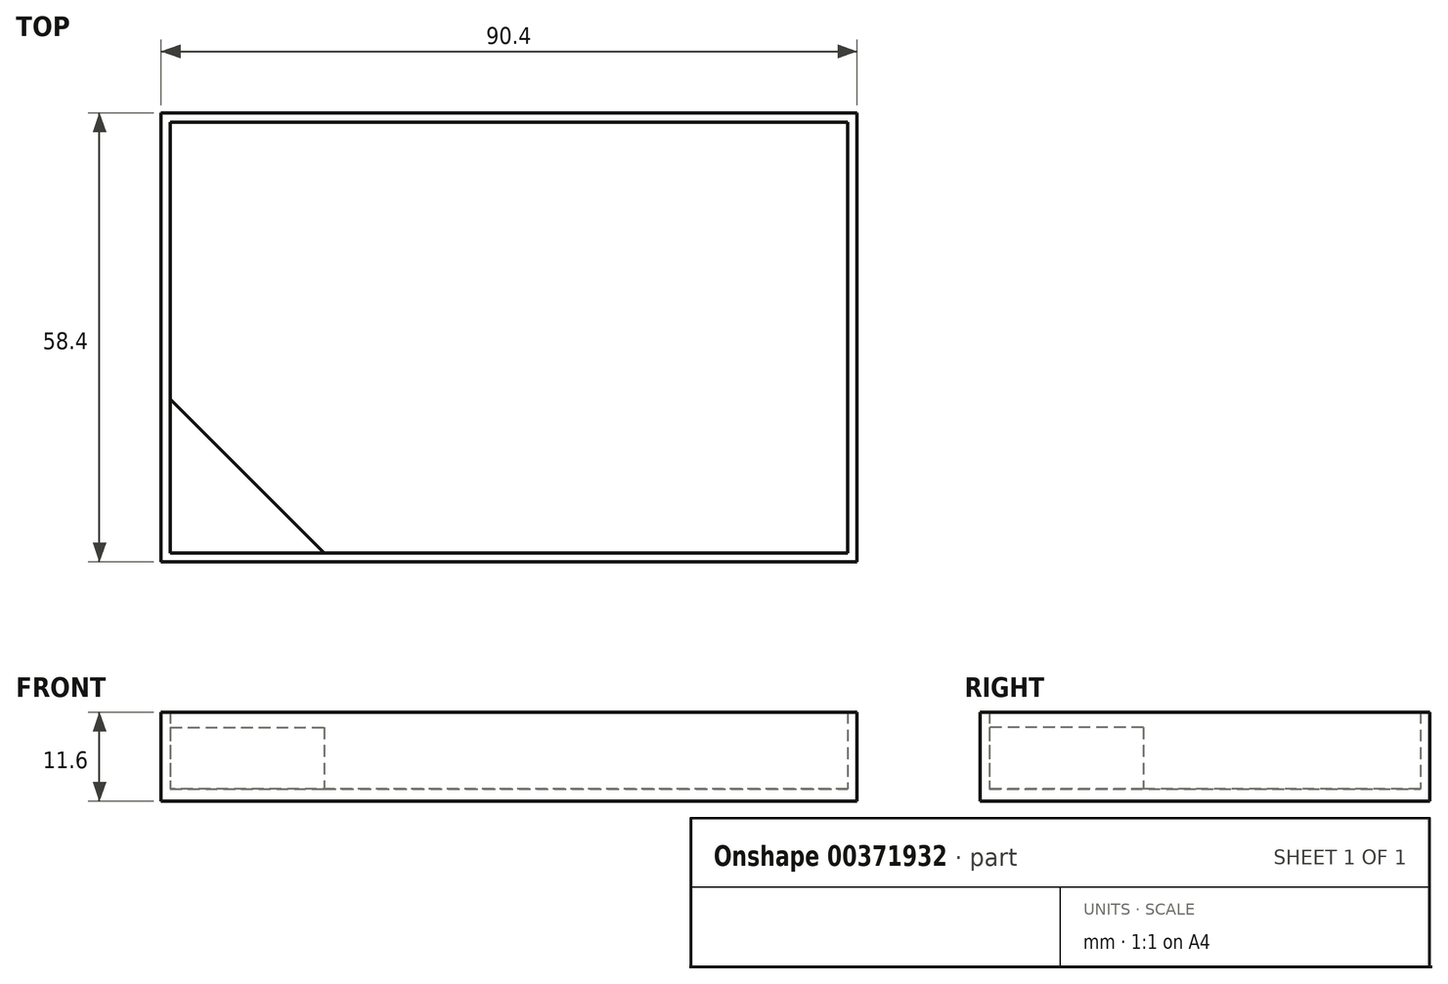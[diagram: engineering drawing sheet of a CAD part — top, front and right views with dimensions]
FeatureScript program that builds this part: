
annotation { "Feature Type Name" : "Feature", "Feature Type Description" : "" }
export const myFeature = defineFeature(function(context is Context, id is Id, definition is map)
    precondition{}
    {
        {
            var Q0;
            Q0=qCreatedBy(makeId("Top.planeOp"),FACE);
            var sketch = newSketch(context, id + "F0", { "sketchPlane" : qUnion([Q0])});
            skLineSegment(sketch, "E0.bottom", {"start": v(44, -28) * mm, "end": v(-44, -28) * mm});
            skLineSegment(sketch, "E0.top", {"start": v(44, 28) * mm, "end": v(-44, 28) * mm});
            skLineSegment(sketch, "E0.left", {"start": v(44, -28) * mm, "end": v(44, 28) * mm});
            skLineSegment(sketch, "E0.right", {"start": v(-44, -28) * mm, "end": v(-44, 28) * mm});
            skPoint(sketch, "E0.middle", {"position": v(0, 0) * mm});
            skLineSegment(sketch, "E1.bottom", {"start": v(-45.2, 29.2) * mm, "end": v(45.2, 29.2) * mm});
            skLineSegment(sketch, "E1.top", {"start": v(-45.2, -29.2) * mm, "end": v(45.2, -29.2) * mm});
            skLineSegment(sketch, "E1.left", {"start": v(-45.2, 29.2) * mm, "end": v(-45.2, -29.2) * mm});
            skLineSegment(sketch, "E1.right", {"start": v(45.2, 29.2) * mm, "end": v(45.2, -29.2) * mm});
            skSolve(sketch);
        }
        {
            var Q0;
            Q0 = qSketchRegion(id + "F0", true);
            var Q1;
            Q1=makeQuery(id+"F0.imprint","IMPRINT",FACE,{"disambiguationData":[TD([[makeQuery(id+"F0.imprint","IMPRINT",EDGE,{"derivedFrom":sQuery(id+"F0.wireOp",EDGE,"E0.bottom")}),-1.0]])]});
            extrude(context, id + "F1", {"entities" : qUnion([Q0, Q1]), "depth" : 1.6 * mm});
        }
        {
            var Q0;
            Q0=makeQuery(id+"F1.opExtrude","CAP_FACE",FACE,{"disambiguationData":[OSD([sQuery(id+"F0.wireOp",EDGE,"E1.bottom"),sQuery(id+"F0.wireOp",EDGE,"E1.top"),sQuery(id+"F0.wireOp",EDGE,"E1.left"),sQuery(id+"F0.wireOp",EDGE,"E1.right")])],"isStart":false});
            var sketch = newSketch(context, id + "F2", { "sketchPlane" : qUnion([Q0])});
            skLineSegment(sketch, "E2.0.0", {"start": v(-45.2, 29.2) * mm, "end": v(-45.2, -29.2) * mm});
            skLineSegment(sketch, "E2.0.1", {"start": v(-45.2, -29.2) * mm, "end": v(45.2, -29.2) * mm});
            skLineSegment(sketch, "E2.0.2", {"start": v(45.2, -29.2) * mm, "end": v(45.2, 29.2) * mm});
            skLineSegment(sketch, "E2.0.3", {"start": v(45.2, 29.2) * mm, "end": v(-45.2, 29.2) * mm});
            skLineSegment(sketch, "E3.0", {"start": v(-44, 28) * mm, "end": v(-44, -28) * mm});
            skLineSegment(sketch, "E3.1", {"start": v(44, 28) * mm, "end": v(-44, 28) * mm});
            skLineSegment(sketch, "E3.2", {"start": v(44, -28) * mm, "end": v(44, 28) * mm});
            skLineSegment(sketch, "E3.3", {"start": v(-44, -28) * mm, "end": v(44, -28) * mm});
            skSolve(sketch);
        }
        {
            var Q0;
            Q0 = qSketchRegion(id + "F2", true);
            extrude(context, id + "F3", {"entities" : qUnion([Q0]), "operationType" : NewBodyOperationType.ADD, "depth" : 10 * mm});
        }
        {
            var Q0;
            Q0=makeQuery(id+"F1.opExtrude","CAP_FACE",FACE,{"disambiguationData":[OSD([sQuery(id+"F0.wireOp",EDGE,"E1.bottom"),sQuery(id+"F0.wireOp",EDGE,"E1.top"),sQuery(id+"F0.wireOp",EDGE,"E1.left"),sQuery(id+"F0.wireOp",EDGE,"E1.right")])],"isStart":false});
            var sketch = newSketch(context, id + "F4", { "sketchPlane" : qUnion([Q0])});
            skLineSegment(sketch, "E4.0.0", {"start": v(-44, 28) * mm, "end": v(-44, -28) * mm});
            skLineSegment(sketch, "E4.0.1", {"start": v(-44, -28) * mm, "end": v(44, -28) * mm});
            skLineSegment(sketch, "E4.0.2", {"start": v(44, -28) * mm, "end": v(44, 28) * mm});
            skLineSegment(sketch, "E4.0.3", {"start": v(44, 28) * mm, "end": v(-44, 28) * mm});
            skLineSegment(sketch, "E5", {"start": v(-44, -8) * mm, "end": v(-24, -28) * mm});
            skSolve(sketch);
        }
        {
            var Q0;
            {var subQ3=sQuery(id+"F4.wireOp",EDGE,"E5");Q0=makeQuery(id+"F4.imprint","IMPRINT",FACE,{"disambiguationData":[TD([[makeQuery(id+"F4.imprint","IMPRINT",EDGE,{"derivedFrom":subQ3}),-1.0]])]});}
            extrude(context, id + "F5", {"entities" : qUnion([Q0]), "operationType" : NewBodyOperationType.ADD, "depth" : 8 * mm});
        }
    });
